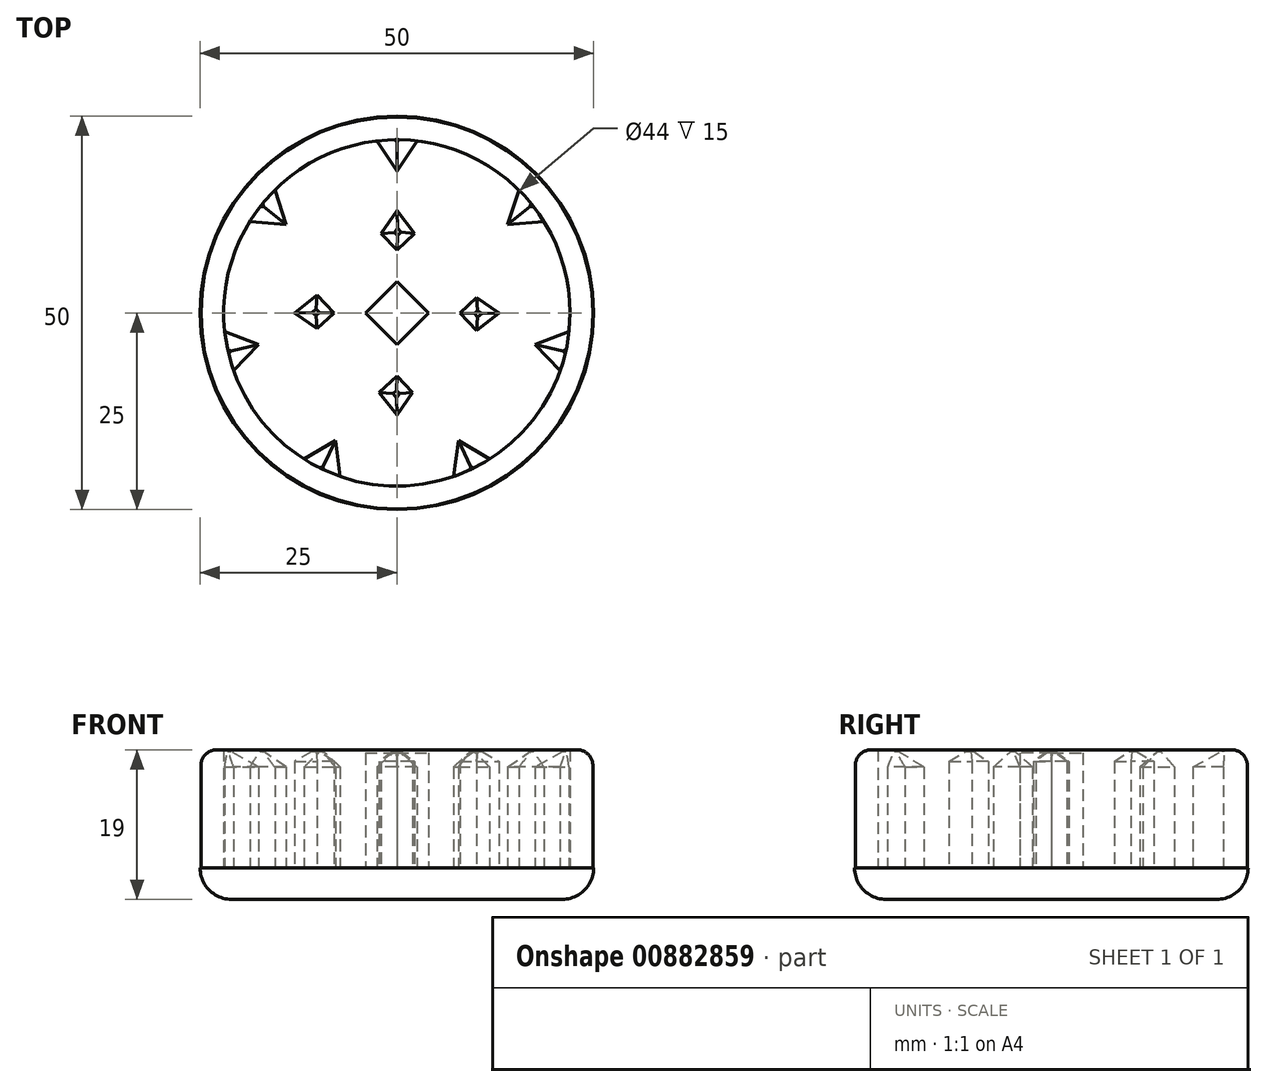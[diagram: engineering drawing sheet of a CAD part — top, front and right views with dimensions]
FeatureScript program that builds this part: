
annotation { "Feature Type Name" : "Feature", "Feature Type Description" : "" }
export const myFeature = defineFeature(function(context is Context, id is Id, definition is map)
    precondition{}
    {
        {
            var Q0;
            Q0=qCreatedBy(makeId("Top.planeOp"),FACE);
            var sketch = newSketch(context, id + "F0", { "sketchPlane" : qUnion([Q0])});
            skCircle(sketch, "E0", {"center": v(0, 0) * mm, "radius": 25 * mm});
            skSolve(sketch);
        }
        {
            var Q0;
            Q0=makeQuery(id+"F0.imprint","IMPRINT",FACE,{"disambiguationData":[TD([[makeQuery(id+"F0.imprint","IMPRINT",EDGE,{"derivedFrom":sQuery(id+"F0.wireOp",EDGE,"E0")}),1.0]])]});
            extrude(context, id + "F1", {"entities" : qUnion([Q0]), "depth" : 4 * mm, "offsetDistance" : 25 * mm});
        }
        {
            var Q0;
            Q0=makeQuery(id+"F1.opExtrude","CAP_FACE",FACE,{"disambiguationData":[OSD([sQuery(id+"F0.wireOp",EDGE,"E0")])],"isStart":false});
            var sketch = newSketch(context, id + "F2", { "sketchPlane" : qUnion([Q0])});
            skCircle(sketch, "E1", {"center": v(0, 0) * mm, "radius": 25 * mm});
            skCircle(sketch, "E2", {"center": v(0, 0) * mm, "radius": 22 * mm});
            skCircle(sketch, "E3", {"center": v(0, 0) * mm, "radius": 4 * mm});
            skCircle(sketch, "E4", {"center": v(0, 0) * mm, "radius": 8 * mm});
            skCircle(sketch, "E5", {"center": v(0, 0) * mm, "radius": 13 * mm});
            skCircle(sketch, "E6", {"center": v(0, 0) * mm, "radius": 18 * mm});
            skLineSegment(sketch, "E7", {"start": v(0, 0) * mm, "end": v(0, -4) * mm});
            skLineSegment(sketch, "E8", {"start": v(0, -4) * mm, "end": v(4, 0) * mm});
            skLineSegment(sketch, "E9", {"start": v(4, 0) * mm, "end": v(0, 4) * mm});
            skLineSegment(sketch, "E10", {"start": v(0, 4) * mm, "end": v(-4, 0) * mm});
            skLineSegment(sketch, "E11", {"start": v(-4, 0) * mm, "end": v(0, -4) * mm});
            skLineSegment(sketch, "E12", {"start": v(0, -13) * mm, "end": v(-2.26, -10.11) * mm});
            skLineSegment(sketch, "E13", {"start": v(-2.26, -10.11) * mm, "end": v(0, -8) * mm});
            skLineSegment(sketch, "E14", {"start": v(0, -8) * mm, "end": v(1.98, -10.11) * mm});
            skLineSegment(sketch, "E15", {"start": v(1.98, -10.11) * mm, "end": v(0, -13) * mm});
            skLineSegment(sketch, "E16", {"start": v(0, 18) * mm, "end": v(2.55, 21.85) * mm});
            skLineSegment(sketch, "E17", {"start": v(0, 18) * mm, "end": v(-2.55, 21.85) * mm});
            skLineSegment(sketch, "E18.1.0", {"start": v(-14.07, 11.22) * mm, "end": v(-18.67, 11.63) * mm});
            skLineSegment(sketch, "E18.1.1", {"start": v(-14.07, 11.22) * mm, "end": v(-15.5, 15.62) * mm});
            skLineSegment(sketch, "E18.2.0", {"start": v(-17.55, -4) * mm, "end": v(-20.74, -7.35) * mm});
            skLineSegment(sketch, "E18.2.1", {"start": v(-17.55, -4) * mm, "end": v(-21.87, -2.38) * mm});
            skLineSegment(sketch, "E18.3.0", {"start": v(-7.8, -16.22) * mm, "end": v(-7.19, -20.8) * mm});
            skLineSegment(sketch, "E18.3.1", {"start": v(-7.8, -16.22) * mm, "end": v(-11.78, -18.58) * mm});
            skLineSegment(sketch, "E18.4.0", {"start": v(7.8, -16.22) * mm, "end": v(11.78, -18.58) * mm});
            skLineSegment(sketch, "E18.4.1", {"start": v(7.8, -16.22) * mm, "end": v(7.19, -20.8) * mm});
            skLineSegment(sketch, "E18.5.0", {"start": v(17.55, -4) * mm, "end": v(21.87, -2.38) * mm});
            skLineSegment(sketch, "E18.5.1", {"start": v(17.55, -4) * mm, "end": v(20.74, -7.35) * mm});
            skLineSegment(sketch, "E18.6.0", {"start": v(14.07, 11.22) * mm, "end": v(15.5, 15.62) * mm});
            skLineSegment(sketch, "E18.6.1", {"start": v(14.07, 11.22) * mm, "end": v(18.67, 11.63) * mm});
            skLineSegment(sketch, "E19.1.0", {"start": v(10.11, -2.26) * mm, "end": v(8, 0) * mm});
            skLineSegment(sketch, "E19.1.1", {"start": v(10.11, 1.98) * mm, "end": v(13, 0) * mm});
            skLineSegment(sketch, "E19.1.2", {"start": v(8, 0) * mm, "end": v(10.11, 1.98) * mm});
            skLineSegment(sketch, "E19.1.3", {"start": v(13, 0) * mm, "end": v(10.11, -2.26) * mm});
            skLineSegment(sketch, "E19.2.0", {"start": v(2.26, 10.11) * mm, "end": v(0, 8) * mm});
            skLineSegment(sketch, "E19.2.1", {"start": v(-1.98, 10.11) * mm, "end": v(0, 13) * mm});
            skLineSegment(sketch, "E19.2.2", {"start": v(0, 8) * mm, "end": v(-1.98, 10.11) * mm});
            skLineSegment(sketch, "E19.2.3", {"start": v(0, 13) * mm, "end": v(2.26, 10.11) * mm});
            skLineSegment(sketch, "E19.3.0", {"start": v(-10.11, 2.26) * mm, "end": v(-8, 0) * mm});
            skLineSegment(sketch, "E19.3.1", {"start": v(-10.11, -1.98) * mm, "end": v(-13, 0) * mm});
            skLineSegment(sketch, "E19.3.2", {"start": v(-8, 0) * mm, "end": v(-10.11, -1.98) * mm});
            skLineSegment(sketch, "E19.3.3", {"start": v(-13, 0) * mm, "end": v(-10.11, 2.26) * mm});
            skSolve(sketch);
        }
        {
            var Q0;
            Q0=makeQuery(id+"F2.imprint","IMPRINT",FACE,{"disambiguationData":[TD([[makeQuery(id+"F2.imprint","IMPRINT",EDGE,{"derivedFrom":sQuery(id+"F2.wireOp",EDGE,"E12")}),-1.0]])]});
            var Q1;
            Q1=makeQuery(id+"F2.imprint","IMPRINT",FACE,{"disambiguationData":[TD([[makeQuery(id+"F2.imprint","IMPRINT",EDGE,{"derivedFrom":sQuery(id+"F2.wireOp",EDGE,"E8")}),1.0]])]});
            var Q2;
            Q2=makeQuery(id+"F2.imprint","IMPRINT",FACE,{"disambiguationData":[TD([[makeQuery(id+"F2.imprint","IMPRINT",EDGE,{"derivedFrom":sQuery(id+"F2.wireOp",EDGE,"B3bonk9R-CgNS-daiu-jhZK-fihJorbaMshz")}),1.0]])]});
            var Q3;
            Q3=makeQuery(id+"F2.imprint","IMPRINT",FACE,{"disambiguationData":[TD([[makeQuery(id+"F2.imprint","IMPRINT",EDGE,{"derivedFrom":sQuery(id+"F2.wireOp",EDGE,"E19.3.0")}),-1.0]])]});
            var Q4;
            Q4=makeQuery(id+"F2.imprint","IMPRINT",FACE,{"disambiguationData":[TD([[makeQuery(id+"F2.imprint","IMPRINT",EDGE,{"derivedFrom":sQuery(id+"F2.wireOp",EDGE,"E19.2.0")}),-1.0]])]});
            var Q5;
            Q5=makeQuery(id+"F2.imprint","IMPRINT",FACE,{"disambiguationData":[TD([[makeQuery(id+"F2.imprint","IMPRINT",EDGE,{"derivedFrom":sQuery(id+"F2.wireOp",EDGE,"E19.1.0")}),-1.0]])]});
            var Q6;
            {var subQ0=sQuery(id+"F2.wireOp",EDGE,"E18.6.0");Q6=makeQuery(id+"F2.imprint","IMPRINT",FACE,{"disambiguationData":[TD([[makeQuery(id+"F2.imprint","IMPRINT",EDGE,{"derivedFrom":subQ0}),-1.0]])]});}
            var Q7;
            {var subQ0=sQuery(id+"F2.wireOp",EDGE,"E18.5.0");Q7=makeQuery(id+"F2.imprint","IMPRINT",FACE,{"disambiguationData":[TD([[makeQuery(id+"F2.imprint","IMPRINT",EDGE,{"derivedFrom":subQ0}),-1.0]])]});}
            var Q8;
            {var subQ0=sQuery(id+"F2.wireOp",EDGE,"E18.4.0");Q8=makeQuery(id+"F2.imprint","IMPRINT",FACE,{"disambiguationData":[TD([[makeQuery(id+"F2.imprint","IMPRINT",EDGE,{"derivedFrom":subQ0}),-1.0]])]});}
            var Q9;
            {var subQ0=sQuery(id+"F2.wireOp",EDGE,"E18.3.0");Q9=makeQuery(id+"F2.imprint","IMPRINT",FACE,{"disambiguationData":[TD([[makeQuery(id+"F2.imprint","IMPRINT",EDGE,{"derivedFrom":subQ0}),-1.0]])]});}
            var Q10;
            {var subQ0=sQuery(id+"F2.wireOp",EDGE,"E18.2.0");Q10=makeQuery(id+"F2.imprint","IMPRINT",FACE,{"disambiguationData":[TD([[makeQuery(id+"F2.imprint","IMPRINT",EDGE,{"derivedFrom":subQ0}),-1.0]])]});}
            var Q11;
            {var subQ0=sQuery(id+"F2.wireOp",EDGE,"E18.1.0");Q11=makeQuery(id+"F2.imprint","IMPRINT",FACE,{"disambiguationData":[TD([[makeQuery(id+"F2.imprint","IMPRINT",EDGE,{"derivedFrom":subQ0}),-1.0]])]});}
            var Q12;
            {var subQ0=sQuery(id+"F2.wireOp",EDGE,"E16");Q12=makeQuery(id+"F2.imprint","IMPRINT",FACE,{"disambiguationData":[TD([[makeQuery(id+"F2.imprint","IMPRINT",EDGE,{"derivedFrom":subQ0}),1.0]])]});}
            extrude(context, id + "F3", {"entities" : qUnion([Q0, Q1, Q2, Q3, Q4, Q5, Q6, Q7, Q8, Q9, Q10, Q11, Q12]), "operationType" : NewBodyOperationType.ADD, "depth" : 14.8 * mm, "offsetDistance" : 25 * mm});
        }
        {
            var Q0;
            Q0=makeQuery(id+"F1.opExtrude","CAP_FACE",FACE,{"disambiguationData":[OSD([sQuery(id+"F0.wireOp",EDGE,"E0")])],"isStart":false});
            var sketch = newSketch(context, id + "F4", { "sketchPlane" : qUnion([Q0])});
            skCircle(sketch, "E20", {"center": v(0, 0) * mm, "radius": 22 * mm});
            skCircle(sketch, "E21", {"center": v(0, 0) * mm, "radius": 24.9 * mm});
            skSolve(sketch);
        }
        {
            var Q0;
            Q0 = qSketchRegion(id + "F4", true);
            extrude(context, id + "F5", {"entities" : qUnion([Q0]), "operationType" : NewBodyOperationType.ADD, "depth" : 15 * mm, "offsetDistance" : 25 * mm});
        }
        {
            var Q0;
            Q0=makeQuery(id+"F3.opExtrude","CAP_FACE",FACE,{"disambiguationData":[OSD([sQuery(id+"F2.wireOp",EDGE,"E19.3.0"),sQuery(id+"F2.wireOp",EDGE,"E19.3.1"),sQuery(id+"F2.wireOp",EDGE,"E19.3.2"),sQuery(id+"F2.wireOp",EDGE,"E19.3.3")])],"isStart":false});
            var Q1;
            Q1=makeQuery(id+"F3.opExtrude","CAP_FACE",FACE,{"disambiguationData":[OSD([sQuery(id+"F2.wireOp",EDGE,"E12"),sQuery(id+"F2.wireOp",EDGE,"E13"),sQuery(id+"F2.wireOp",EDGE,"E14"),sQuery(id+"F2.wireOp",EDGE,"E15")])],"isStart":false});
            var Q2;
            Q2=makeQuery(id+"F3.opExtrude","CAP_FACE",FACE,{"disambiguationData":[OSD([sQuery(id+"F2.wireOp",EDGE,"E19.1.0"),sQuery(id+"F2.wireOp",EDGE,"E19.1.1"),sQuery(id+"F2.wireOp",EDGE,"E19.1.2"),sQuery(id+"F2.wireOp",EDGE,"E19.1.3")])],"isStart":false});
            var Q3;
            Q3=makeQuery(id+"F3.opExtrude","CAP_FACE",FACE,{"disambiguationData":[OSD([sQuery(id+"F2.wireOp",EDGE,"E19.2.0"),sQuery(id+"F2.wireOp",EDGE,"E19.2.1"),sQuery(id+"F2.wireOp",EDGE,"E19.2.2"),sQuery(id+"F2.wireOp",EDGE,"E19.2.3")])],"isStart":false});
            chamfer(context, id + "F6", {"entities" : qUnion([Q0, Q1, Q2, Q3]), "width" : 1.3 * mm, "tangentPropagation" : true});
        }
        {
            var Q0;
            Q0=makeQuery(id+"F3.opExtrude","CAP_EDGE",EDGE,{"disambiguationData":[OSD([sQuery(id+"F2.wireOp",EDGE,"E18.6.0")])],"isStart":false});
            var Q1;
            Q1=makeQuery(id+"F3.opExtrude","CAP_EDGE",EDGE,{"disambiguationData":[OSD([sQuery(id+"F2.wireOp",EDGE,"E18.6.1")])],"isStart":false});
            var Q2;
            Q2=makeQuery(id+"F3.opExtrude","CAP_EDGE",EDGE,{"disambiguationData":[OSD([sQuery(id+"F2.wireOp",EDGE,"E18.5.0")])],"isStart":false});
            var Q3;
            Q3=makeQuery(id+"F3.opExtrude","CAP_EDGE",EDGE,{"disambiguationData":[OSD([sQuery(id+"F2.wireOp",EDGE,"E18.5.1")])],"isStart":false});
            var Q4;
            Q4=makeQuery(id+"F3.opExtrude","CAP_EDGE",EDGE,{"disambiguationData":[OSD([sQuery(id+"F2.wireOp",EDGE,"E18.4.0")])],"isStart":false});
            var Q5;
            Q5=makeQuery(id+"F3.opExtrude","CAP_EDGE",EDGE,{"disambiguationData":[OSD([sQuery(id+"F2.wireOp",EDGE,"E18.4.1")])],"isStart":false});
            var Q6;
            Q6=makeQuery(id+"F3.opExtrude","CAP_EDGE",EDGE,{"disambiguationData":[OSD([sQuery(id+"F2.wireOp",EDGE,"E18.3.1")])],"isStart":false});
            var Q7;
            Q7=makeQuery(id+"F3.opExtrude","CAP_EDGE",EDGE,{"disambiguationData":[OSD([sQuery(id+"F2.wireOp",EDGE,"E18.3.0")])],"isStart":false});
            var Q8;
            Q8=makeQuery(id+"F3.opExtrude","CAP_EDGE",EDGE,{"disambiguationData":[OSD([sQuery(id+"F2.wireOp",EDGE,"E18.2.0")])],"isStart":false});
            var Q9;
            Q9=makeQuery(id+"F3.opExtrude","CAP_EDGE",EDGE,{"disambiguationData":[OSD([sQuery(id+"F2.wireOp",EDGE,"E18.2.1")])],"isStart":false});
            var Q10;
            Q10=makeQuery(id+"F3.opExtrude","CAP_EDGE",EDGE,{"disambiguationData":[OSD([sQuery(id+"F2.wireOp",EDGE,"E18.1.0")])],"isStart":false});
            var Q11;
            Q11=makeQuery(id+"F3.opExtrude","CAP_EDGE",EDGE,{"disambiguationData":[OSD([sQuery(id+"F2.wireOp",EDGE,"E17")])],"isStart":false});
            var Q12;
            Q12=makeQuery(id+"F3.opExtrude","CAP_EDGE",EDGE,{"disambiguationData":[OSD([sQuery(id+"F2.wireOp",EDGE,"E16")])],"isStart":false});
            var Q13;
            Q13=makeQuery(id+"F3.opExtrude","CAP_EDGE",EDGE,{"disambiguationData":[OSD([sQuery(id+"F2.wireOp",EDGE,"E18.1.1")])],"isStart":false});
            chamfer(context, id + "F7", {"entities" : qUnion([Q0, Q1, Q2, Q3, Q4, Q5, Q6, Q7, Q8, Q9, Q10, Q11, Q12, Q13]), "width" : 2 * mm, "tangentPropagation" : true});
        }
        {
            var Q0;
            Q0=makeQuery(id+"F1.opExtrude","CAP_EDGE",EDGE,{"disambiguationData":[OSD([sQuery(id+"F0.wireOp",EDGE,"E0")])],"isStart":true});
            fillet(context, id + "F8", {"entities" : qUnion([Q0]), "radius" : 4 * mm, "tangentPropagation" : true, "allowEdgeOverflow" : false});
        }
        {
            var Q0;
            Q0=makeQuery(id+"F5.opExtrude","CAP_EDGE",EDGE,{"disambiguationData":[OSD([sQuery(id+"F4.wireOp",EDGE,"E21")])],"isStart":false});
            fillet(context, id + "F9", {"entities" : qUnion([Q0]), "radius" : 2 * mm, "tangentPropagation" : true, "allowEdgeOverflow" : false});
        }
        {
            var Q0;
            Q0=makeQuery(id+"F3.opExtrude","CAP_FACE",FACE,{"disambiguationData":[OSD([sQuery(id+"F2.wireOp",EDGE,"E8"),sQuery(id+"F2.wireOp",EDGE,"E9"),sQuery(id+"F2.wireOp",EDGE,"E10"),sQuery(id+"F2.wireOp",EDGE,"E11")])],"isStart":false});
            var sketch = newSketch(context, id + "F10", { "sketchPlane" : qUnion([Q0])});
            skCircle(sketch, "E22", {"center": v(0, 0) * mm, "radius": 4.56 * mm});
            skSolve(sketch);
        }
        {
            var Q0;
            Q0 = qSketchRegion(id + "F10", true);
            extrude(context, id + "F11", {"entities" : qUnion([Q0]), "operationType" : NewBodyOperationType.REMOVE, "oppositeDirection" : true, "depth" : .2 * mm, "offsetDistance" : 25 * mm});
        }
    });
